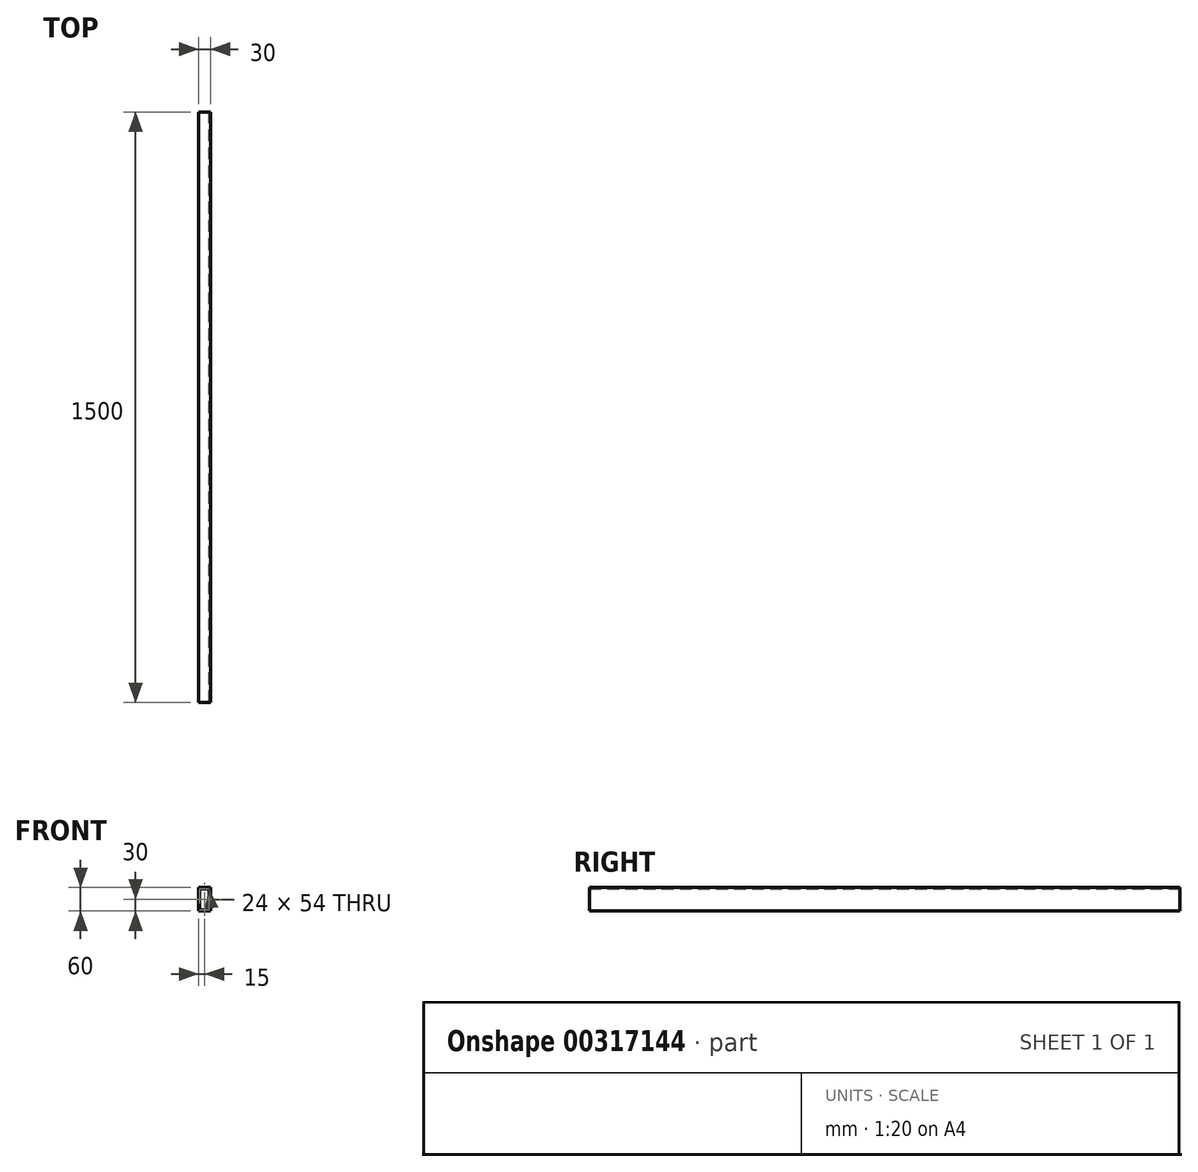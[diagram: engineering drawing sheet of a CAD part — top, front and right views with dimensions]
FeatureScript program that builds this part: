
annotation { "Feature Type Name" : "Feature", "Feature Type Description" : "" }
export const myFeature = defineFeature(function(context is Context, id is Id, definition is map)
    precondition{}
    {
        {
            var Q0;
            Q0=qCreatedBy(makeId("Front.planeOp"),FACE);
            var sketch = newSketch(context, id + "F0", { "sketchPlane" : qUnion([Q0])});
            skLineSegment(sketch, "E0.bottom", {"start": v(15, 30) * mm, "end": v(-15, 30) * mm});
            skLineSegment(sketch, "E0.top", {"start": v(15, -30) * mm, "end": v(-15, -30) * mm});
            skLineSegment(sketch, "E0.left", {"start": v(15, 30) * mm, "end": v(15, -30) * mm});
            skLineSegment(sketch, "E0.right", {"start": v(-15, 30) * mm, "end": v(-15, -30) * mm});
            skPoint(sketch, "E0.middle", {"position": v(0, 0) * mm});
            skLineSegment(sketch, "E1.0", {"start": v(12, -27) * mm, "end": v(-12, -27) * mm});
            skLineSegment(sketch, "E1.1", {"start": v(12, 27) * mm, "end": v(12, -27) * mm});
            skLineSegment(sketch, "E1.2", {"start": v(12, 27) * mm, "end": v(-12, 27) * mm});
            skLineSegment(sketch, "E1.3", {"start": v(-12, 27) * mm, "end": v(-12, -27) * mm});
            skSolve(sketch);
        }
        {
            var Q0;
            Q0=makeQuery(id+"F0.imprint","IMPRINT",FACE,{"disambiguationData":[TD([[makeQuery(id+"F0.imprint","IMPRINT",EDGE,{"derivedFrom":sQuery(id+"F0.wireOp",EDGE,"E0.bottom")}),1.0]])]});
            extrude(context, id + "F1", {"entities" : qUnion([Q0]), "endBound" : BoundingType.SYMMETRIC, "depth" : 1500 * mm});
        }
    });
